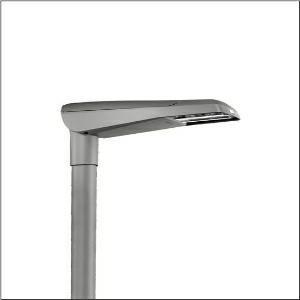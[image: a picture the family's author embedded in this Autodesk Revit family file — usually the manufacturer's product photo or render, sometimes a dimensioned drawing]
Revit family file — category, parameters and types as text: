
# Revit family: streetlight_sl_11_iq_micro___st1_2a_5xc1a31f08ce_a0bf
name_source: partatom
category: Lighting Fixtures
units: mm (PartAtom-declared; Revit-internal decimal feet)

## family parameters
Cut with Voids When Loaded = No
Host = Face
Light Source = No
Part Type = Normal
Room Calculation Point = No
Round Connector Dimension = Use Diameter
Shared = No

## types (1)
- --- (1 x LED, 1620 lm, 12.6 W, 3000K)
    Apparent Load = 13 VA
    CIE Flux Codes = 33 71 96 100 100
    Color Rendering = 80
    Color Temperature = 3000K
    Default Elevation = 1800 mm
    Description = Streetlight SL 11 iQ micro, mast luminaire, primary light control with 3 zone facetted reflector, of plastic, silver coated, highly specular, primary optical cover: cover, of PMMA, transparent, light distribution: ST1.2a, light emission: direct distribution, primary light characteristic: asymmetric, installation type: post-top, side-entry, lamps: LED, High Power LED, rated values: 1.620lm | 12,6W | 128,6lm/W (begin service life); end service life: 1.620lm | 12,9W; at 50% lumin. flux: 810lm | 6,8W | 119,1lm/W, colour temperature: 3000K, colour rendering: CRI > 80, light colour: 830, light setting 1 begin service life: 100% | 1.620lm | 12,6W | 128,6lm/W | 3.000K, light setting 1 end service life: 12,9W, further light settings possible, control: Street-Remote, optimised constant luminous flux control (CLO 2.0), Desk-Remote (wireless, voltage-free reading and setting of iQ features in the workshop via application-optimized NFC function/RFID function), Light-Fading, Smart-Wire, Night-Set, Lumen-Switch, Temp-Guard, Auto-Match, with cable H07RN-F 5x 1.5mm², mains connection: 230..240V, AC, 50/60Hz, connection cable pre-assembled, cable length: 5,5m, luminaire housing, of diecast aluminium, powder-coated, Siteco® metallic grey (DB 702S), please order mast flange separately, inclination adjustable without tools: 0°, 5°, 10°, 15° (post-top) | 0°, -5°, -10°, -15° (side-entry), sealing non-destructively replaceable, multi-level sealing system, length: 600mm, width: 174mm, height: 116mm, mast flange for spigot size: 42mm (side-entry): 5XC10008XM4, 60/48mm (side-entry/post-top): 5XC10108XM2, 76/60mm (side-entry/post-top): 5XC10108XM1, equipment: standard, protection rating (complete): IP66, insulation class (complete): insulation class II (safety insulation), certification: CE, ENEC, ENEC+, VDE, impact resistance: IK10, permissible operating ambient temperature for outdoor applications: -25..+50°C, standard-compliant lighting for roads and squares, Environmental Product Declaration (EPD) tested and certified by an independent institute, packaging unit: 1 piece

Light Distribution: ST1.2a
    Height = 116 mm
    Lamp = 1 x LED
    Lamp Light Flux = 1620 lm
    Lamp Power = 12.6 W
    Lamp count = 1
    Length = 600 mm
    Luminous efficacy = 129 lm/W
    Manufacturer = Siteco
    ModVariant = No
    Model = 5XC1A31F08CE
    Number of Poles = 1
    OnlyDefault = Yes
    Power Factor = 1
    Product Name = Streetlight SL 11 iQ micro | ST1.2a
    Product group = mast luminaire | pylon top
    ProductGroupID = 6100
    Protection Class = Protection class II
    Protection Degree = IP 66
    RLX_Detail_Level = 1
    RLX_Emergency_Light_Flux = 0 lm
    RLX_Emergency_Type = 0
    RLX_Emergency_Type_DB = No
    RlxData = <blob elided: 26553 chars, md5=2ce35fe3>
    Socket = socket
    Standby Power = 0 W
    System Light Flux = 1620 lm
    System Power = 13 W
    Type Comments = factory setting: luminous flux: 100 % | dim-lin: 254 | 229 mA
    Type Image = l_1006566.jpg
    URL = http://relux.com
    VarID = @adj_017979
    Voltage = 0 V
    Weight = 0.00 kg
    Width = 174 mm

## geometry (parser evidence)
native form markers: Blend x4, Sweep x10
no freeform markers — native parametric forms only
